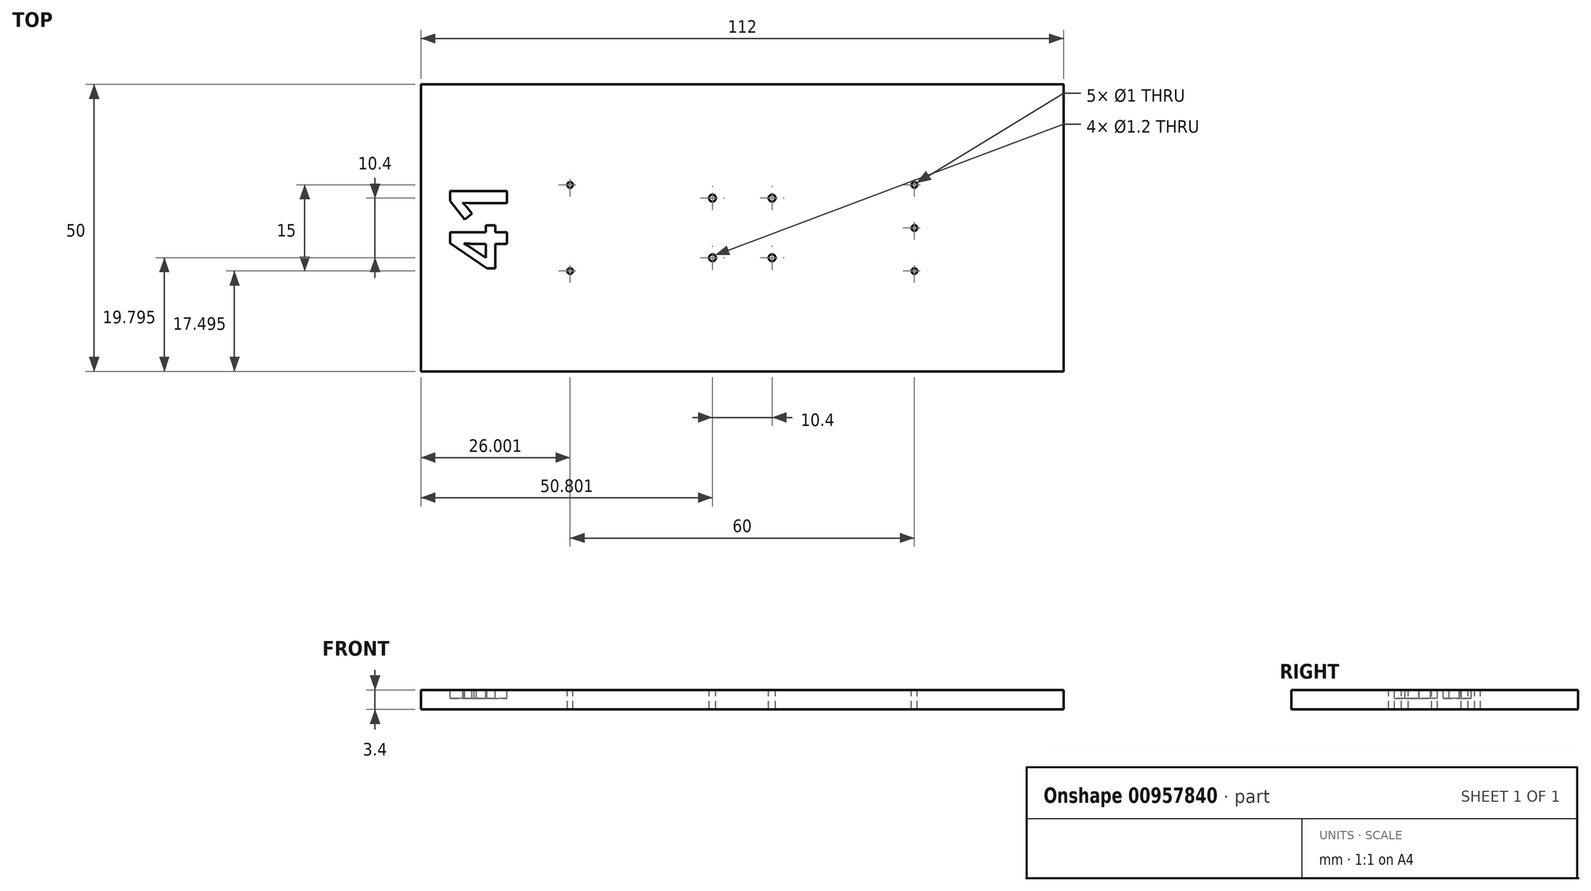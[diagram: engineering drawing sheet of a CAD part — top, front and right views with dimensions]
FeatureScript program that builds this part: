
annotation { "Feature Type Name" : "Feature", "Feature Type Description" : "" }
export const myFeature = defineFeature(function(context is Context, id is Id, definition is map)
    precondition{}
    {
        {
            var Q0;
            Q0=qCreatedBy(makeId("Top.planeOp"),FACE);
            var sketch = newSketch(context, id + "F0", { "sketchPlane" : qUnion([Q0])});
            skLineSegment(sketch, "E0.bottom", {"start": v(-43.16, 28.34) * mm, "end": v(68.84, 28.34) * mm});
            skLineSegment(sketch, "E0.top", {"start": v(-43.16, -21.66) * mm, "end": v(68.84, -21.66) * mm});
            skLineSegment(sketch, "E0.left", {"start": v(-43.16, 28.34) * mm, "end": v(-43.16, -21.66) * mm});
            skLineSegment(sketch, "E0.right", {"start": v(68.84, 28.34) * mm, "end": v(68.84, -21.66) * mm});
            skSolve(sketch);
        }
        {
            var Q0;
            Q0=makeQuery(id+"F0.imprint","IMPRINT",FACE,{"disambiguationData":[TD([[makeQuery(id+"F0.imprint","IMPRINT",EDGE,{"derivedFrom":sQuery(id+"F0.wireOp",EDGE,"E0.bottom")}),-1.0]])]});
            extrude(context, id + "F1", {"entities" : qUnion([Q0]), "depth" : 3.4 * mm, "offsetDistance" : 25 * mm});
        }
        {
            var Q0;
            Q0=makeQuery(id+"F1.opExtrude","CAP_FACE",FACE,{"disambiguationData":[OSD([sQuery(id+"F0.wireOp",EDGE,"E0.bottom"),sQuery(id+"F0.wireOp",EDGE,"E0.top"),sQuery(id+"F0.wireOp",EDGE,"E0.left"),sQuery(id+"F0.wireOp",EDGE,"E0.right")])],"isStart":false});
            var sketch = newSketch(context, id + "F2", { "sketchPlane" : qUnion([Q0])});
            skText(sketch, "E1", { "text": "41", "fontName": "OpenSans-Bold.ttf"});
            const initialGuessF2  = {"E1": [-0.02816, -0.00391, 0, 1, 0.01]};
            skSetInitialGuess(sketch, initialGuessF2);
            skSolve(sketch);
        }
        {
            var Q0;
            Q0=qSketchRegion(id+"F2",true);
            extrude(context, id + "F3", {"entities" : qUnion([Q0]), "operationType" : NewBodyOperationType.REMOVE, "oppositeDirection" : true, "depth" : 1.5 * mm, "offsetDistance" : 25 * mm});
        }
        {
            var Q0;
            {var subQ0=sQuery(id+"F0.wireOp",EDGE,"E0.left");var subQ1=sQuery(id+"F0.wireOp",EDGE,"E0.bottom");var subQ2=sQuery(id+"F0.wireOp",EDGE,"E0.right");var subQ3=sQuery(id+"F0.wireOp",EDGE,"E0.top");Q0=makeQuery(id+"F3.boolean.opBoolean","SPLIT",FACE,{"disambiguationData":[TD([makeQuery(id+"F1.opExtrude","SWEPT_FACE",FACE,{"disambiguationData":[OSD([subQ1])]})])],"derivedFrom":makeQuery(id+"F1.opExtrude","CAP_FACE",FACE,{"disambiguationData":[OSD([subQ1,subQ3,subQ0,subQ2])],"isStart":false})});}
            var sketch = newSketch(context, id + "F4", { "sketchPlane" : qUnion([Q0])});
            skLineSegment(sketch, "E2.bottom", {"start": v(-23.16, -13.16) * mm, "end": v(48.84, -13.16) * mm});
            skLineSegment(sketch, "E2.top", {"start": v(-23.16, 19.84) * mm, "end": v(48.84, 19.84) * mm});
            skLineSegment(sketch, "E2.left", {"start": v(-23.16, -13.16) * mm, "end": v(-23.16, 19.84) * mm});
            skLineSegment(sketch, "E2.right", {"start": v(48.84, -13.16) * mm, "end": v(48.84, 19.84) * mm});
            skCircle(sketch, "E3", {"center": v(42.84, 3.34) * mm, "radius": 0.5 * mm});
            skCircle(sketch, "E4", {"center": v(42.84, 10.84) * mm, "radius": 0.5 * mm});
            skCircle(sketch, "E5", {"center": v(42.84, -4.16) * mm, "radius": 0.5 * mm});
            skCircle(sketch, "E6", {"center": v(-17.16, -4.16) * mm, "radius": 0.5 * mm});
            skCircle(sketch, "E7", {"center": v(-17.16, 10.84) * mm, "radius": 0.5 * mm});
            skCircle(sketch, "E8", {"center": v(18.04, 8.54) * mm, "radius": 0.6 * mm});
            skCircle(sketch, "E9", {"center": v(18.04, -1.86) * mm, "radius": 0.6 * mm});
            skCircle(sketch, "E10", {"center": v(7.64, -1.86) * mm, "radius": 0.6 * mm});
            skCircle(sketch, "E11", {"center": v(7.64, 8.54) * mm, "radius": 0.6 * mm});
            skSolve(sketch);
        }
        {
            var Q0;
            Q0=makeQuery(id+"F4.imprint","IMPRINT",FACE,{"disambiguationData":[TD([[makeQuery(id+"F4.imprint","IMPRINT",EDGE,{"derivedFrom":sQuery(id+"F4.wireOp",EDGE,"E7")}),1.0]])]});
            var Q1;
            Q1=makeQuery(id+"F4.imprint","IMPRINT",FACE,{"disambiguationData":[TD([[makeQuery(id+"F4.imprint","IMPRINT",EDGE,{"derivedFrom":sQuery(id+"F4.wireOp",EDGE,"E6")}),1.0]])]});
            var Q2;
            Q2=makeQuery(id+"F4.imprint","IMPRINT",FACE,{"disambiguationData":[TD([[makeQuery(id+"F4.imprint","IMPRINT",EDGE,{"derivedFrom":sQuery(id+"F4.wireOp",EDGE,"E11")}),1.0]])]});
            var Q3;
            Q3=makeQuery(id+"F4.imprint","IMPRINT",FACE,{"disambiguationData":[TD([[makeQuery(id+"F4.imprint","IMPRINT",EDGE,{"derivedFrom":sQuery(id+"F4.wireOp",EDGE,"E8")}),1.0]])]});
            var Q4;
            Q4=makeQuery(id+"F4.imprint","IMPRINT",FACE,{"disambiguationData":[TD([[makeQuery(id+"F4.imprint","IMPRINT",EDGE,{"derivedFrom":sQuery(id+"F4.wireOp",EDGE,"E9")}),1.0]])]});
            var Q5;
            Q5=makeQuery(id+"F4.imprint","IMPRINT",FACE,{"disambiguationData":[TD([[makeQuery(id+"F4.imprint","IMPRINT",EDGE,{"derivedFrom":sQuery(id+"F4.wireOp",EDGE,"E10")}),1.0]])]});
            var Q6;
            Q6=makeQuery(id+"F4.imprint","IMPRINT",FACE,{"disambiguationData":[TD([[makeQuery(id+"F4.imprint","IMPRINT",EDGE,{"derivedFrom":sQuery(id+"F4.wireOp",EDGE,"E4")}),1.0]])]});
            var Q7;
            Q7=makeQuery(id+"F4.imprint","IMPRINT",FACE,{"disambiguationData":[TD([[makeQuery(id+"F4.imprint","IMPRINT",EDGE,{"derivedFrom":sQuery(id+"F4.wireOp",EDGE,"E3")}),1.0]])]});
            var Q8;
            Q8=makeQuery(id+"F4.imprint","IMPRINT",FACE,{"disambiguationData":[TD([[makeQuery(id+"F4.imprint","IMPRINT",EDGE,{"derivedFrom":sQuery(id+"F4.wireOp",EDGE,"E5")}),1.0]])]});
            extrude(context, id + "F5", {"entities" : qUnion([Q0, Q1, Q2, Q3, Q4, Q5, Q6, Q7, Q8]), "operationType" : NewBodyOperationType.REMOVE, "endBound" : BoundingType.UP_TO_NEXT, "oppositeDirection" : true, "depth" : 25 * mm, "offsetDistance" : 25 * mm});
        }
    });
